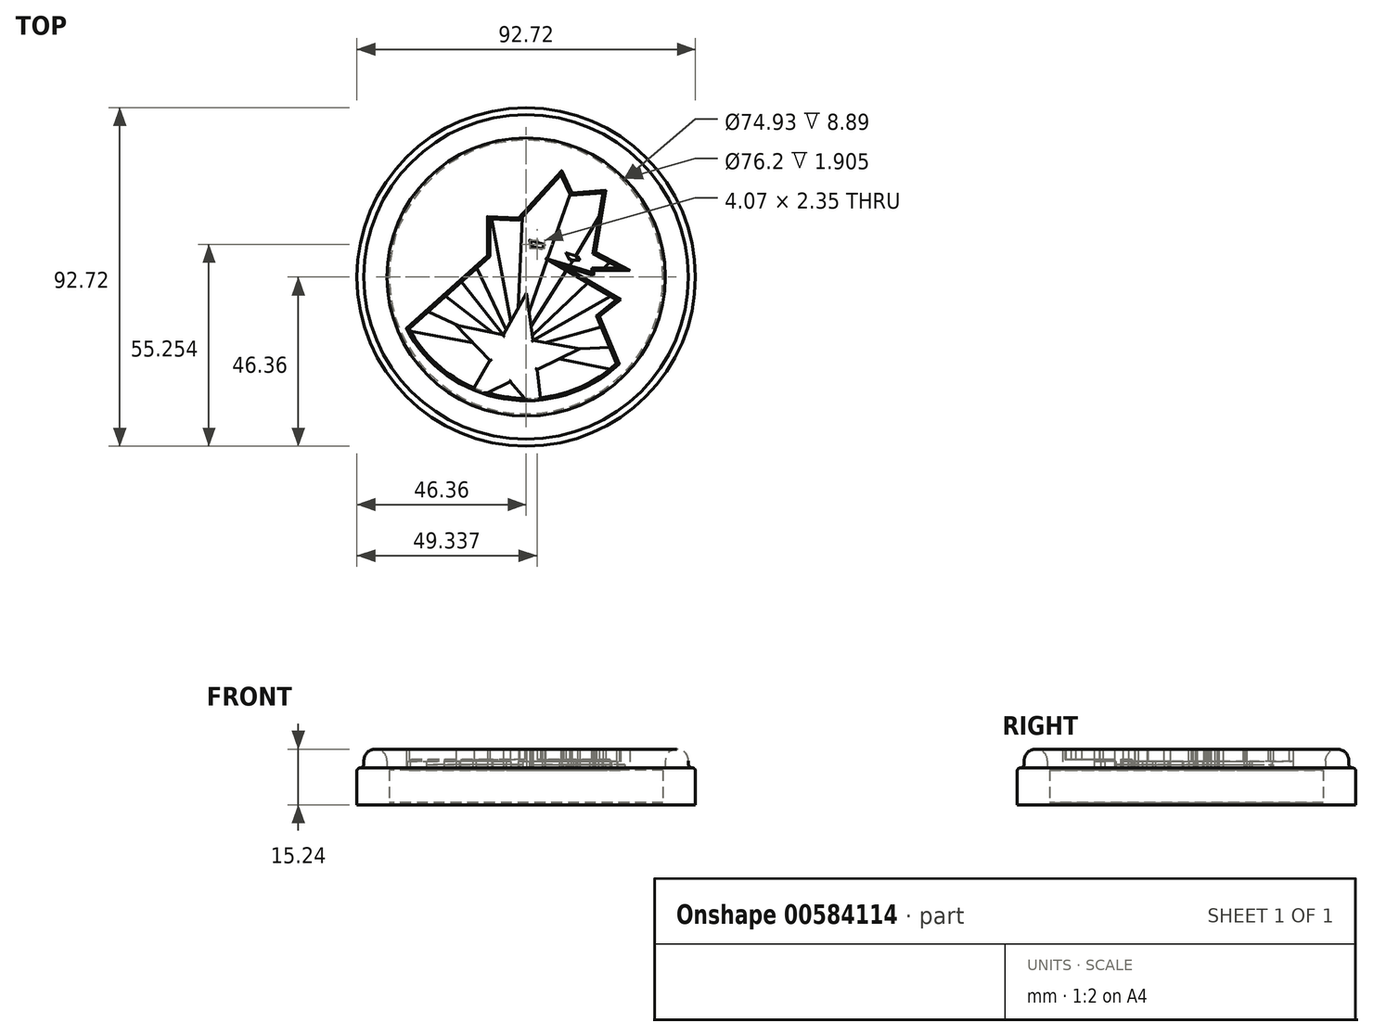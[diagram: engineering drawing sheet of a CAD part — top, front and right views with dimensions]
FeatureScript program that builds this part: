
annotation { "Feature Type Name" : "Feature", "Feature Type Description" : "" }
export const myFeature = defineFeature(function(context is Context, id is Id, definition is map)
    precondition{}
    {
        {
            var Q0;
            Q0=qCreatedBy(makeId("Top.planeOp"),FACE);
            var sketch = newSketch(context, id + "F0", { "sketchPlane" : qUnion([Q0])});
            skCircle(sketch, "E0", {"center": v(0, 0) * mm, "radius": 38.1 * mm});
            skCircle(sketch, "E1", {"center": v(0, 0) * mm, "radius": 44.45 * mm});
            skCircle(sketch, "E2", {"center": v(0, 0) * mm, "radius": 46.35 * mm});
            skSolve(sketch);
        }
        {
            var Q0;
            Q0=makeQuery(id+"F0.imprint","IMPRINT",FACE,{"disambiguationData":[TD([[makeQuery(id+"F0.imprint","IMPRINT",EDGE,{"derivedFrom":sQuery(id+"F0.wireOp",EDGE,"E0")}),1.0]])]});
            extrude(context, id + "F1", {"entities" : qUnion([Q0]), "depth" : 10.16 * mm, "offsetDistance" : 25.4 * mm});
        }
        {
            var Q0;
            Q0=makeQuery(id+"F1.opExtrude","CAP_FACE",FACE,{"disambiguationData":[OSD([sQuery(id+"F0.wireOp",EDGE,"E0")])],"isStart":false});
            var sketch = newSketch(context, id + "F2", { "sketchPlane" : qUnion([Q0])});
            skArc(sketch, "E3", {"start": v(-32.85, -14.11) * mm, "mid": v(-6.09, -33.4) * mm, "end": v(25.5, -23.88) * mm});
            skLineSegment(sketch, "E4", {"start": v(-32.85, -14.11) * mm, "end": v(-10.58, 5.84) * mm});
            skLineSegment(sketch, "E5", {"start": v(-10.58, 5.84) * mm, "end": v(-10.58, 16.55) * mm});
            skLineSegment(sketch, "E6", {"start": v(-10.58, 16.55) * mm, "end": v(-4.83, 12.59) * mm});
            skLineSegment(sketch, "E7", {"start": v(-4.83, 12.59) * mm, "end": v(-10.58, 16.55) * mm});
            skLineSegment(sketch, "E8", {"start": v(-10.58, 16.55) * mm, "end": v(-2.03, 16.14) * mm});
            skLineSegment(sketch, "E9", {"start": v(-2.03, 16.14) * mm, "end": v(9.72, 29.13) * mm});
            skLineSegment(sketch, "E10", {"start": v(9.72, 29.13) * mm, "end": v(12.54, 22.98) * mm});
            skLineSegment(sketch, "E11", {"start": v(12.54, 22.98) * mm, "end": v(21.76, 23.72) * mm});
            skLineSegment(sketch, "E12", {"start": v(21.76, 23.72) * mm, "end": v(18.98, 6.7) * mm});
            skLineSegment(sketch, "E13", {"start": v(18.98, 6.7) * mm, "end": v(28.37, 1.78) * mm});
            skLineSegment(sketch, "E14", {"start": v(28.37, 1.78) * mm, "end": v(18.58, 1.78) * mm});
            skLineSegment(sketch, "E15", {"start": v(18.58, 1.78) * mm, "end": v(18.37, 0.46) * mm});
            skLineSegment(sketch, "E16", {"start": v(18.37, 0.46) * mm, "end": v(10.24, 2.93) * mm});
            skLineSegment(sketch, "E17", {"start": v(10.24, 2.93) * mm, "end": v(25.84, -6.19) * mm});
            skLineSegment(sketch, "E18", {"start": v(25.84, -6.19) * mm, "end": v(20, -10.8) * mm});
            skLineSegment(sketch, "E19", {"start": v(20, -10.8) * mm, "end": v(25.5, -23.88) * mm});
            skSolve(sketch);
        }
        {
            var Q0;
            Q0=makeQuery(id+"F2.imprint","IMPRINT",FACE,{"disambiguationData":[TD([[makeQuery(id+"F2.imprint","IMPRINT",EDGE,{"derivedFrom":sQuery(id+"F2.wireOp",EDGE,"E3")}),1.0]])]});
            var sketch = newSketch(context, id + "F3", { "sketchPlane" : qUnion([Q0])});
            skLineSegment(sketch, "E20", {"start": v(0.94, 10.07) * mm, "end": v(1.33, 8.38) * mm});
            skLineSegment(sketch, "E21", {"start": v(1.33, 8.38) * mm, "end": v(4.45, 7.72) * mm});
            skLineSegment(sketch, "E22", {"start": v(4.45, 7.72) * mm, "end": v(5.01, 8.87) * mm});
            skLineSegment(sketch, "E23", {"start": v(5.01, 8.87) * mm, "end": v(0.94, 10.07) * mm});
            skLineSegment(sketch, "E24", {"start": v(10.84, 6.63) * mm, "end": v(11.92, 4.63) * mm});
            skLineSegment(sketch, "E25", {"start": v(11.92, 4.63) * mm, "end": v(14.64, 4.63) * mm});
            skLineSegment(sketch, "E26", {"start": v(14.64, 4.63) * mm, "end": v(14.08, 5.57) * mm});
            skLineSegment(sketch, "E27", {"start": v(14.08, 5.57) * mm, "end": v(10.84, 6.63) * mm});
            skLineSegment(sketch, "E28", {"start": v(-14.6, -30.83) * mm, "end": v(-10, -22.83) * mm});
            skLineSegment(sketch, "E29", {"start": v(-10, -22.83) * mm, "end": v(-19.25, -13.22) * mm});
            skLineSegment(sketch, "E30", {"start": v(-19.25, -13.22) * mm, "end": v(-6.27, -15.89) * mm});
            skLineSegment(sketch, "E31", {"start": v(-6.27, -15.89) * mm, "end": v(0.13, -4.45) * mm});
            skLineSegment(sketch, "E32", {"start": v(0.13, -4.45) * mm, "end": v(1.9, -17.38) * mm});
            skLineSegment(sketch, "E33", {"start": v(1.9, -17.38) * mm, "end": v(14.64, -19.73) * mm});
            skLineSegment(sketch, "E34", {"start": v(14.64, -19.73) * mm, "end": v(3.03, -25.35) * mm});
            skLineSegment(sketch, "E35", {"start": v(3.03, -25.35) * mm, "end": v(3.91, -33.66) * mm});
            skLineSegment(sketch, "E36", {"start": v(3.91, -33.66) * mm, "end": v(0.13, -33.86) * mm});
            skLineSegment(sketch, "E37", {"start": v(0.13, -33.86) * mm, "end": v(-4.38, -28.7) * mm});
            skLineSegment(sketch, "E38", {"start": v(-4.38, -28.7) * mm, "end": v(-11.24, -32) * mm});
            skLineSegment(sketch, "E39", {"start": v(-11.24, -32) * mm, "end": v(-14.6, -30.83) * mm});
            skLineSegment(sketch, "E40", {"start": v(-14.62, -18.02) * mm, "end": v(-32.49, -14.69) * mm});
            skLineSegment(sketch, "E41", {"start": v(-32.49, -14.69) * mm, "end": v(-32.85, -14.12) * mm});
            skLineSegment(sketch, "E42", {"start": v(-32.85, -14.12) * mm, "end": v(-27.28, -9.33) * mm});
            skLineSegment(sketch, "E43", {"start": v(-27.28, -9.33) * mm, "end": v(-18.32, -13.4) * mm});
            skArc(sketch, "E44", {"start": v(-32.49, -14.69) * mm, "mid": v(-24.65, -23.98) * mm, "end": v(-14.6, -30.83) * mm});
            skLineSegment(sketch, "E45", {"start": v(-9.23, -15.28) * mm, "end": v(-22.47, -4.92) * mm});
            skLineSegment(sketch, "E46", {"start": v(-22.47, -4.92) * mm, "end": v(-27.28, -9.33) * mm});
            skLineSegment(sketch, "E47", {"start": v(-6.27, -15.89) * mm, "end": v(-18.07, -0.95) * mm});
            skLineSegment(sketch, "E48", {"start": v(-18.07, -0.95) * mm, "end": v(-22.47, -4.92) * mm});
            skLineSegment(sketch, "E49", {"start": v(-5.48, -14.46) * mm, "end": v(-13.71, 3.02) * mm});
            skLineSegment(sketch, "E50", {"start": v(-13.71, 3.02) * mm, "end": v(-18.07, -0.95) * mm});
            skLineSegment(sketch, "E51", {"start": v(-4.16, -12.12) * mm, "end": v(-9.46, 15.78) * mm});
            skLineSegment(sketch, "E52", {"start": v(-9.46, 15.78) * mm, "end": v(-10.55, 16.52) * mm});
            skLineSegment(sketch, "E53", {"start": v(-10.55, 16.52) * mm, "end": v(-10.55, 5.84) * mm});
            skLineSegment(sketch, "E54", {"start": v(-10.55, 5.84) * mm, "end": v(-13.71, 3.02) * mm});
            skLineSegment(sketch, "E55", {"start": v(-2.18, -8.58) * mm, "end": v(-0.98, 17.28) * mm});
            skLineSegment(sketch, "E56", {"start": v(-0.98, 17.28) * mm, "end": v(-2.04, 16.14) * mm});
            skLineSegment(sketch, "E57", {"start": v(-2.04, 16.14) * mm, "end": v(-10.55, 16.52) * mm});
            skLineSegment(sketch, "E58", {"start": v(0.8, -9.33) * mm, "end": v(12.28, 23.53) * mm});
            skLineSegment(sketch, "E59", {"start": v(12.28, 23.53) * mm, "end": v(9.72, 29.12) * mm});
            skLineSegment(sketch, "E60", {"start": v(9.72, 29.12) * mm, "end": v(-0.98, 17.28) * mm});
            skLineSegment(sketch, "E61", {"start": v(1.37, -13.5) * mm, "end": v(11.34, 2.27) * mm});
            skLineSegment(sketch, "E62", {"start": v(11.34, 2.27) * mm, "end": v(10.18, 2.96) * mm});
            skLineSegment(sketch, "E63", {"start": v(10.18, 2.96) * mm, "end": v(11.5, 2.58) * mm});
            skLineSegment(sketch, "E64", {"start": v(11.5, 2.58) * mm, "end": v(12.96, 4.63) * mm});
            skLineSegment(sketch, "E65", {"start": v(13.61, 5.72) * mm, "end": v(20.77, 17.86) * mm});
            skLineSegment(sketch, "E66", {"start": v(20.77, 17.86) * mm, "end": v(21.73, 23.72) * mm});
            skLineSegment(sketch, "E67", {"start": v(21.73, 23.72) * mm, "end": v(12.53, 22.96) * mm});
            skLineSegment(sketch, "E68", {"start": v(12.53, 22.96) * mm, "end": v(12.28, 23.53) * mm});
            skLineSegment(sketch, "E69", {"start": v(1.72, -15.99) * mm, "end": v(17.31, -1.22) * mm});
            skLineSegment(sketch, "E70", {"start": v(17.31, -1.22) * mm, "end": v(11.34, 2.27) * mm});
            skLineSegment(sketch, "E71", {"start": v(11.5, 2.58) * mm, "end": v(18.29, 0.58) * mm});
            skLineSegment(sketch, "E72", {"start": v(18.29, 0.58) * mm, "end": v(18.52, 1.84) * mm});
            skLineSegment(sketch, "E73", {"start": v(18.52, 1.84) * mm, "end": v(20.77, 1.84) * mm});
            skLineSegment(sketch, "E74", {"start": v(20.77, 1.84) * mm, "end": v(23.32, 4.42) * mm});
            skLineSegment(sketch, "E75", {"start": v(23.32, 4.42) * mm, "end": v(18.91, 6.71) * mm});
            skLineSegment(sketch, "E76", {"start": v(18.91, 6.71) * mm, "end": v(20.77, 17.86) * mm});
            skLineSegment(sketch, "E77", {"start": v(20.77, 1.84) * mm, "end": v(26.96, 2) * mm});
            skLineSegment(sketch, "E78", {"start": v(26.96, 2) * mm, "end": v(23.32, 4.42) * mm});
            skLineSegment(sketch, "E79", {"start": v(1.9, -17.38) * mm, "end": v(23.32, -5.13) * mm});
            skLineSegment(sketch, "E80", {"start": v(23.32, -5.13) * mm, "end": v(17.31, -1.22) * mm});
            skLineSegment(sketch, "E81", {"start": v(23.32, -5.13) * mm, "end": v(25.05, -6.1) * mm});
            skLineSegment(sketch, "E82", {"start": v(25.05, -6.1) * mm, "end": v(19.8, -10.88) * mm});
            skLineSegment(sketch, "E83", {"start": v(19.8, -10.88) * mm, "end": v(21, -13.5) * mm});
            skLineSegment(sketch, "E84", {"start": v(21, -13.5) * mm, "end": v(5.2, -17.98) * mm});
            skLineSegment(sketch, "E85", {"start": v(14.64, -19.73) * mm, "end": v(22.92, -19.3) * mm});
            skLineSegment(sketch, "E86", {"start": v(22.92, -19.3) * mm, "end": v(21, -13.5) * mm});
            skLineSegment(sketch, "E87", {"start": v(22.92, -19.3) * mm, "end": v(24.85, -23.52) * mm});
            skLineSegment(sketch, "E88", {"start": v(24.85, -23.52) * mm, "end": v(22.92, -25.27) * mm});
            skLineSegment(sketch, "E89", {"start": v(22.92, -25.27) * mm, "end": v(9.08, -22.42) * mm});
            skArc(sketch, "E90", {"start": v(-11.24, -32) * mm, "mid": v(-5.63, -33.42) * mm, "end": v(0.13, -33.86) * mm});
            skArc(sketch, "E91", {"start": v(3.91, -33.66) * mm, "mid": v(14.1, -31.01) * mm, "end": v(22.92, -25.27) * mm});
            skSolve(sketch);
        }
        {
            var Q0;
            Q0=makeQuery(id+"F2.imprint","IMPRINT",FACE,{"disambiguationData":[TD([[makeQuery(id+"F2.imprint","IMPRINT",EDGE,{"derivedFrom":sQuery(id+"F2.wireOp",EDGE,"E3")}),1.0]])]});
            extrude(context, id + "F4", {"entities" : qUnion([Q0]), "operationType" : NewBodyOperationType.ADD, "depth" : 5.08 * mm, "offsetDistance" : 25.4 * mm});
        }
        {
            var Q0;
            Q0=makeQuery(id+"F4.opExtrude","CAP_FACE",FACE,{"disambiguationData":[OSD([sQuery(id+"F2.wireOp",EDGE,"E3"),sQuery(id+"F2.wireOp",EDGE,"E4"),sQuery(id+"F2.wireOp",EDGE,"E5"),sQuery(id+"F2.wireOp",EDGE,"E8"),sQuery(id+"F2.wireOp",EDGE,"E9"),sQuery(id+"F2.wireOp",EDGE,"E10"),sQuery(id+"F2.wireOp",EDGE,"E11"),sQuery(id+"F2.wireOp",EDGE,"E12"),sQuery(id+"F2.wireOp",EDGE,"E13"),sQuery(id+"F2.wireOp",EDGE,"E14"),sQuery(id+"F2.wireOp",EDGE,"E15"),sQuery(id+"F2.wireOp",EDGE,"E16"),sQuery(id+"F2.wireOp",EDGE,"E17"),sQuery(id+"F2.wireOp",EDGE,"E18"),sQuery(id+"F2.wireOp",EDGE,"E19")])],"isStart":false});
            shell(context, id + "F5", {"entities" : qUnion([Q0]), "thickness" : 0.64 * mm});
        }
        {
            var Q0;
            Q0=makeQuery(id+"F3.imprint","IMPRINT",FACE,{"disambiguationData":[TD([[makeQuery(id+"F3.imprint","IMPRINT",EDGE,{"derivedFrom":sQuery(id+"F3.wireOp",EDGE,"E28")}),-1.0]])]});
            var Q1;
            Q1=makeQuery(id+"F3.imprint","IMPRINT",FACE,{"disambiguationData":[TD([[makeQuery(id+"F3.imprint","IMPRINT",EDGE,{"derivedFrom":sQuery(id+"F3.wireOp",EDGE,"E20")}),1.0]])]});
            var Q2;
            Q2=makeQuery(id+"F3.imprint","IMPRINT",FACE,{"disambiguationData":[TD([[makeQuery(id+"F3.imprint","IMPRINT",EDGE,{"derivedFrom":sQuery(id+"F3.wireOp",EDGE,"E24")}),1.0]])]});
            extrude(context, id + "F6", {"entities" : qUnion([Q0, Q1, Q2]), "operationType" : NewBodyOperationType.ADD, "depth" : 5.08 * mm, "offsetDistance" : 25.4 * mm});
        }
        {
            var Q0;
            Q0=makeQuery(id+"F0.imprint","IMPRINT",FACE,{"disambiguationData":[TD([[makeQuery(id+"F0.imprint","IMPRINT",EDGE,{"derivedFrom":sQuery(id+"F0.wireOp",EDGE,"E0")}),-1.0]])]});
            extrude(context, id + "F7", {"entities" : qUnion([Q0]), "operationType" : NewBodyOperationType.ADD, "depth" : 15.24 * mm, "offsetDistance" : 25.4 * mm});
        }
        {
            var Q0;
            Q0=makeQuery(id+"F0.imprint","IMPRINT",FACE,{"disambiguationData":[TD([[makeQuery(id+"F0.imprint","IMPRINT",EDGE,{"derivedFrom":sQuery(id+"F0.wireOp",EDGE,"E1")}),-1.0]])]});
            extrude(context, id + "F8", {"entities" : qUnion([Q0]), "operationType" : NewBodyOperationType.ADD, "depth" : 10.16 * mm, "offsetDistance" : 25.4 * mm});
        }
        {
            var Q0;
            Q0=makeQuery(id+"F7.opExtrude","CAP_EDGE",EDGE,{"disambiguationData":[OSD([sQuery(id+"F0.wireOp",EDGE,"E0")])],"isStart":false});
            var Q1;
            Q1=makeQuery(id+"F7.opExtrude","CAP_EDGE",EDGE,{"disambiguationData":[OSD([sQuery(id+"F0.wireOp",EDGE,"E1")])],"isStart":false});
            fillet(context, id + "F9", {"entities" : qUnion([Q0, Q1]), "radius" : 3.17 * mm, "tangentPropagation" : true, "allowEdgeOverflow" : false});
        }
        {
            var Q0;
            Q0=makeQuery(id+"F6.boolean.opBoolean","MERGE",FACE,{"derivedFrom":[makeQuery(id+"F4.opExtrude","CAP_FACE",FACE,{"disambiguationData":[OSD([sQuery(id+"F2.wireOp",EDGE,"E3"),sQuery(id+"F2.wireOp",EDGE,"E4"),sQuery(id+"F2.wireOp",EDGE,"E5"),sQuery(id+"F2.wireOp",EDGE,"E8"),sQuery(id+"F2.wireOp",EDGE,"E9"),sQuery(id+"F2.wireOp",EDGE,"E10"),sQuery(id+"F2.wireOp",EDGE,"E11"),sQuery(id+"F2.wireOp",EDGE,"E12"),sQuery(id+"F2.wireOp",EDGE,"E13"),sQuery(id+"F2.wireOp",EDGE,"E14"),sQuery(id+"F2.wireOp",EDGE,"E15"),sQuery(id+"F2.wireOp",EDGE,"E16"),sQuery(id+"F2.wireOp",EDGE,"E17"),sQuery(id+"F2.wireOp",EDGE,"E18"),sQuery(id+"F2.wireOp",EDGE,"E19")])],"isStart":false}),makeQuery(id+"F6.opExtrude","CAP_FACE",FACE,{"disambiguationData":[OSD([sQuery(id+"F3.wireOp",EDGE,"E28"),sQuery(id+"F3.wireOp",EDGE,"E29"),sQuery(id+"F3.wireOp",EDGE,"E30"),sQuery(id+"F3.wireOp",EDGE,"E31"),sQuery(id+"F3.wireOp",EDGE,"E32"),sQuery(id+"F3.wireOp",EDGE,"E33"),sQuery(id+"F3.wireOp",EDGE,"E34"),sQuery(id+"F3.wireOp",EDGE,"E35"),sQuery(id+"F3.wireOp",EDGE,"E36"),sQuery(id+"F3.wireOp",EDGE,"E37"),sQuery(id+"F3.wireOp",EDGE,"E38"),sQuery(id+"F3.wireOp",EDGE,"E39")])],"isStart":false})]});
            fillet(context, id + "F10", {"entities" : qUnion([Q0]), "radius" : 0.43 * mm, "tangentPropagation" : true, "allowEdgeOverflow" : false});
        }
        {
            var Q0;
            Q0=makeQuery(id+"F6.opExtrude","CAP_EDGE",EDGE,{"disambiguationData":[OSD([sQuery(id+"F3.wireOp",EDGE,"E21")])],"isStart":false});
            var Q1;
            Q1=makeQuery(id+"F6.opExtrude","CAP_EDGE",EDGE,{"disambiguationData":[OSD([sQuery(id+"F3.wireOp",EDGE,"E22")])],"isStart":false});
            var Q2;
            Q2=makeQuery(id+"F6.opExtrude","CAP_EDGE",EDGE,{"disambiguationData":[OSD([sQuery(id+"F3.wireOp",EDGE,"E23")])],"isStart":false});
            var Q3;
            Q3=makeQuery(id+"F6.opExtrude","CAP_EDGE",EDGE,{"disambiguationData":[OSD([sQuery(id+"F3.wireOp",EDGE,"E20")])],"isStart":false});
            var Q4;
            Q4=makeQuery(id+"F6.opExtrude","CAP_EDGE",EDGE,{"disambiguationData":[OSD([sQuery(id+"F3.wireOp",EDGE,"E24")])],"isStart":false});
            var Q5;
            Q5=makeQuery(id+"F6.opExtrude","CAP_EDGE",EDGE,{"disambiguationData":[OSD([sQuery(id+"F3.wireOp",EDGE,"E27")])],"isStart":false});
            var Q6;
            Q6=makeQuery(id+"F6.opExtrude","CAP_EDGE",EDGE,{"disambiguationData":[OSD([sQuery(id+"F3.wireOp",EDGE,"E26")])],"isStart":false});
            var Q7;
            Q7=makeQuery(id+"F6.opExtrude","CAP_EDGE",EDGE,{"disambiguationData":[OSD([sQuery(id+"F3.wireOp",EDGE,"E25")])],"isStart":false});
            fillet(context, id + "F11", {"entities" : qUnion([Q0, Q1, Q2, Q3, Q4, Q5, Q6, Q7]), "radius" : 0.43 * mm, "tangentPropagation" : true, "allowEdgeOverflow" : false});
        }
        {
            var Q0;
            Q0=makeQuery(id+"F8.opExtrude","CAP_FACE",FACE,{"disambiguationData":[OSD([sQuery(id+"F0.wireOp",EDGE,"E1"),sQuery(id+"F0.wireOp",EDGE,"E2")])],"isStart":false});
            var Q1;
            Q1=makeQuery(id+"F1.opExtrude","CAP_EDGE",EDGE,{"disambiguationData":[OSD([sQuery(id+"F0.wireOp",EDGE,"E0")])],"isStart":false});
            fillet(context, id + "F12", {"entities" : qUnion([Q0, Q1]), "radius" : 0.95 * mm, "tangentPropagation" : true, "allowEdgeOverflow" : false});
        }
        {
            var Q0;
            {var subQ0=sQuery(id+"F3.wireOp",EDGE,"E28");Q0=makeQuery(id+"F3.imprint","IMPRINT",FACE,{"disambiguationData":[TD([[makeQuery(id+"F3.imprint","IMPRINT",EDGE,{"derivedFrom":subQ0}),1.0]])]});}
            var Q1;
            Q1=makeQuery(id+"F3.imprint","IMPRINT",FACE,{"disambiguationData":[TD([[makeQuery(id+"F3.imprint","IMPRINT",EDGE,{"derivedFrom":sQuery(id+"F3.wireOp",EDGE,"E37")}),1.0]])]});
            var Q2;
            {var subQ0=sQuery(id+"F3.wireOp",EDGE,"E35");Q2=makeQuery(id+"F3.imprint","IMPRINT",FACE,{"disambiguationData":[TD([[makeQuery(id+"F3.imprint","IMPRINT",EDGE,{"derivedFrom":subQ0}),1.0]])]});}
            extrude(context, id + "F13", {"entities" : qUnion([Q0, Q1, Q2]), "operationType" : NewBodyOperationType.ADD, "depth" : 2.3 * mm, "offsetDistance" : 25.4 * mm});
        }
        {
            var Q0;
            {var subQ1=sQuery(id+"F3.wireOp",EDGE,"E40");Q0=makeQuery(id+"F3.imprint","IMPRINT",FACE,{"disambiguationData":[TD([[makeQuery(id+"F3.imprint","IMPRINT",EDGE,{"derivedFrom":subQ1}),-1.0]])]});}
            var Q1;
            {var subQ2=sQuery(id+"F3.wireOp",EDGE,"E45");Q1=makeQuery(id+"F3.imprint","IMPRINT",FACE,{"disambiguationData":[TD([[makeQuery(id+"F3.imprint","IMPRINT",EDGE,{"derivedFrom":subQ2}),-1.0]])]});}
            var Q2;
            {var subQ1=sQuery(id+"F3.wireOp",EDGE,"E49");Q2=makeQuery(id+"F3.imprint","IMPRINT",FACE,{"disambiguationData":[TD([[makeQuery(id+"F3.imprint","IMPRINT",EDGE,{"derivedFrom":subQ1}),-1.0]])]});}
            var Q3;
            Q3=makeQuery(id+"F3.imprint","IMPRINT",FACE,{"disambiguationData":[TD([[makeQuery(id+"F3.imprint","IMPRINT",EDGE,{"derivedFrom":sQuery(id+"F3.wireOp",EDGE,"E20")}),-1.0]])]});
            var Q4;
            {var subQ0=sQuery(id+"F3.wireOp",EDGE,"E61");Q4=makeQuery(id+"F3.imprint","IMPRINT",FACE,{"disambiguationData":[TD([[makeQuery(id+"F3.imprint","IMPRINT",EDGE,{"derivedFrom":subQ0}),-1.0]])]});}
            var Q5;
            {var subQ0=sQuery(id+"F3.wireOp",EDGE,"E26");Q5=makeQuery(id+"F3.imprint","IMPRINT",FACE,{"disambiguationData":[TD([[makeQuery(id+"F3.imprint","IMPRINT",EDGE,{"derivedFrom":subQ0}),-1.0]])]});}
            var Q6;
            {var subQ0=sQuery(id+"F3.wireOp",EDGE,"E79");Q6=makeQuery(id+"F3.imprint","IMPRINT",FACE,{"disambiguationData":[TD([[makeQuery(id+"F3.imprint","IMPRINT",EDGE,{"derivedFrom":subQ0}),-1.0]])]});}
            var Q7;
            {var subQ0=sQuery(id+"F3.wireOp",EDGE,"E85");Q7=makeQuery(id+"F3.imprint","IMPRINT",FACE,{"disambiguationData":[TD([[makeQuery(id+"F3.imprint","IMPRINT",EDGE,{"derivedFrom":subQ0}),-1.0]])]});}
            extrude(context, id + "F14", {"entities" : qUnion([Q0, Q1, Q2, Q3, Q4, Q5, Q6, Q7]), "depth" : 1.78 * mm, "offsetDistance" : 25.4 * mm});
        }
        {
            var Q0;
            {var subQ0=sQuery(id+"F3.wireOp",EDGE,"E43");Q0=makeQuery(id+"F3.imprint","IMPRINT",FACE,{"disambiguationData":[TD([[makeQuery(id+"F3.imprint","IMPRINT",EDGE,{"derivedFrom":subQ0}),1.0]])]});}
            var Q1;
            {var subQ0=sQuery(id+"F3.wireOp",EDGE,"E47");Q1=makeQuery(id+"F3.imprint","IMPRINT",FACE,{"disambiguationData":[TD([[makeQuery(id+"F3.imprint","IMPRINT",EDGE,{"derivedFrom":subQ0}),-1.0]])]});}
            var Q2;
            {var subQ1=sQuery(id+"F3.wireOp",EDGE,"E51");Q2=makeQuery(id+"F3.imprint","IMPRINT",FACE,{"disambiguationData":[TD([[makeQuery(id+"F3.imprint","IMPRINT",EDGE,{"derivedFrom":subQ1}),-1.0]])]});}
            var Q3;
            {var subQ3=sQuery(id+"F3.wireOp",EDGE,"E24");Q3=makeQuery(id+"F3.imprint","IMPRINT",FACE,{"disambiguationData":[TD([[makeQuery(id+"F3.imprint","IMPRINT",EDGE,{"derivedFrom":subQ3}),-1.0]])]});}
            var Q4;
            {var subQ2=sQuery(id+"F3.wireOp",EDGE,"E69");Q4=makeQuery(id+"F3.imprint","IMPRINT",FACE,{"disambiguationData":[TD([[makeQuery(id+"F3.imprint","IMPRINT",EDGE,{"derivedFrom":subQ2}),-1.0]])]});}
            var Q5;
            {var subQ2=sQuery(id+"F3.wireOp",EDGE,"E84");Q5=makeQuery(id+"F3.imprint","IMPRINT",FACE,{"disambiguationData":[TD([[makeQuery(id+"F3.imprint","IMPRINT",EDGE,{"derivedFrom":subQ2}),1.0]])]});}
            var Q6;
            Q6=makeQuery(id+"F3.imprint","IMPRINT",FACE,{"disambiguationData":[TD([[makeQuery(id+"F3.imprint","IMPRINT",EDGE,{"derivedFrom":sQuery(id+"F3.wireOp",EDGE,"E74")}),-1.0]])]});
            extrude(context, id + "F15", {"entities" : qUnion([Q0, Q1, Q2, Q3, Q4, Q5, Q6]), "depth" : 0.89 * mm, "offsetDistance" : 25.4 * mm});
        }
    });
